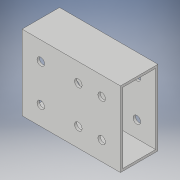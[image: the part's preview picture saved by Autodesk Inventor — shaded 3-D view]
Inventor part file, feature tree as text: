
AUTODESK INVENTOR PART (.ipt)
format: ipt  version: 2018 (Build 220112000, 112)  size: 126,976 bytes
history: native  units: in
note: dims shown in document units (in); Inventor stores cm internally (conversion verified against a paired STEP export)
features: hole x6, extrude x1, shell x1, sketch x1
ambient origin geometry x8: Origin, YZ Plane, XZ Plane, XY Plane, X Axis, Y Axis, Z Axis, Center Point
bodies: Solid1 (feature_tree)
feature tree (9):
  extrude  "Extrusion1"  Depth=1.0in
  shell  "Shell1"  Thickness=2.625in
  hole  "Hole1"  [1 undecoded]
  hole  "Hole2"  [1 undecoded]
  hole  "Hole3"  [1 undecoded]
  hole  "Hole4"  [1 undecoded]
  hole  "Hole5"  [1 undecoded]
  hole  "Hole6"  [1 undecoded]
  sketch  "Sketch1"  dims[d0=2.0in d1=1.0in d2=2.625in d3=0.0in d4=0.0625in d5=0.5in d6=0.5in d7=0.2031in d8=0.75in d9=0.375in d10=0.25in d11=0.5635in d12=1.0in d13=0.8108in d14=0.5in d15=0.5in d16=0.2031in d17=0.75in d18=0.375in d19=0.25in d20=0.5635in d21=1.0in d22=0.8108in d23=0.5in d24=0.5in d25=0.2031in d26=0.75in d27=0.375in d28=0.25in d29=0.5635in d30=1.0in d31=0.8108in d32=0.5in d33=0.5in d34=0.2031in d35=0.75in d36=0.375in d37=0.25in d38=0.5635in d39=1.0in d40=0.8108in d41=0.5in d42=1.5in d43=0.2031in d44=0.75in d45=0.375in d46=0.25in d47=0.5635in d48=1.0in d49=0.8108in d50=0.5in d51=1.5in d52=0.2031in d53=0.75in d54=0.375in d55=0.25in d56=0.5635in d57=1.0in d58=0.8108in]
note: 6 required parameter values undecoded (feature->parameter linkage not recoverable at this tier; creation-order binding heuristic only, values carry confidence <= 0.55)
